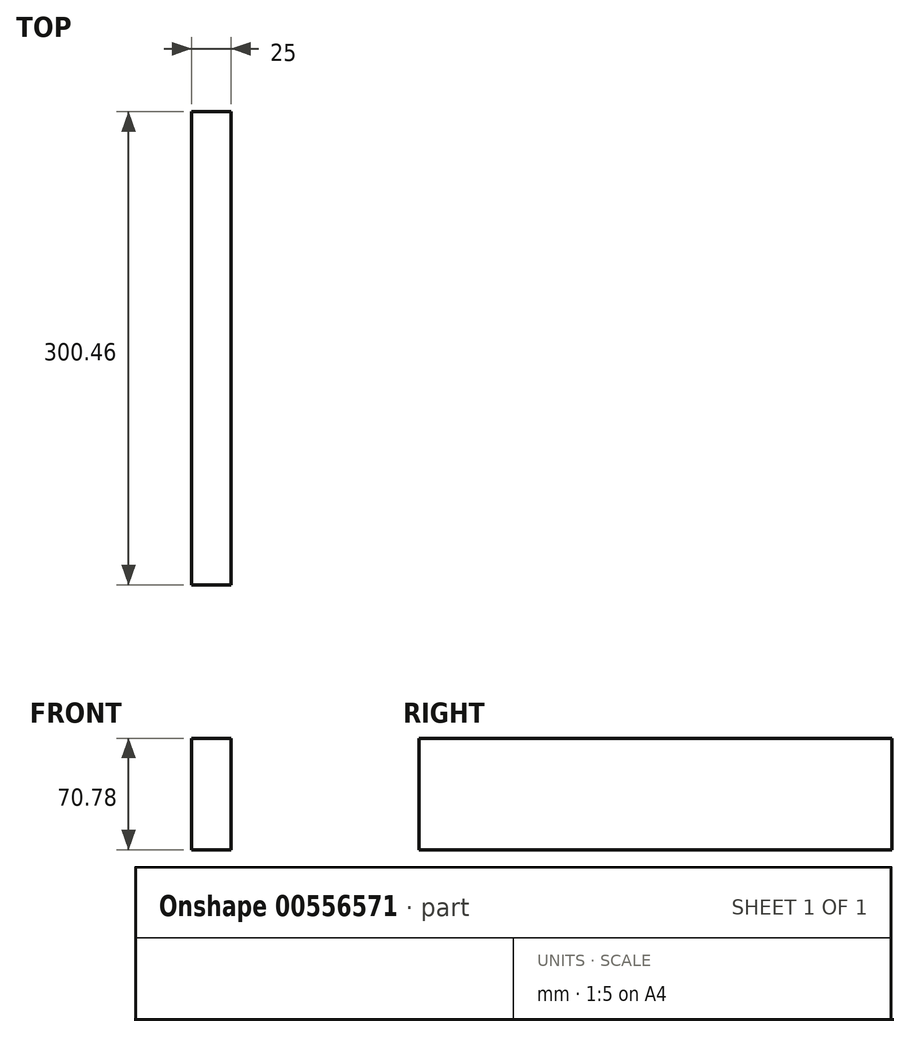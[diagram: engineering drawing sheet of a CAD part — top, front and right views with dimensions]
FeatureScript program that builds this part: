
annotation { "Feature Type Name" : "Feature", "Feature Type Description" : "" }
export const myFeature = defineFeature(function(context is Context, id is Id, definition is map)
    precondition{}
    {
        {
            var Q0;
            Q0=qCreatedBy(makeId("Right.planeOp"),FACE);
            var sketch = newSketch(context, id + "F0", { "sketchPlane" : qUnion([Q0])});
            skLineSegment(sketch, "E0", {"start": v(-154.03, 9.58) * mm, "end": v(146.43, 9.58) * mm});
            skLineSegment(sketch, "E1", {"start": v(-154.03, 9.58) * mm, "end": v(-154.03, -61.2) * mm});
            skLineSegment(sketch, "E2", {"start": v(-154.03, -61.2) * mm, "end": v(146.43, -61.2) * mm});
            skLineSegment(sketch, "E3", {"start": v(146.43, 9.58) * mm, "end": v(146.43, -61.2) * mm});
            skSolve(sketch);
        }
        {
            var Q0;
            Q0=makeQuery(id+"F0.imprint","IMPRINT",FACE,{"disambiguationData":[TD([[makeQuery(id+"F0.imprint","IMPRINT",EDGE,{"derivedFrom":sQuery(id+"F0.wireOp",EDGE,"E0")}),-1.0]])]});
            extrude(context, id + "F1", {"entities" : qUnion([Q0]), "depth" : 25 * mm, "offsetDistance" : 25 * mm});
        }
    });
